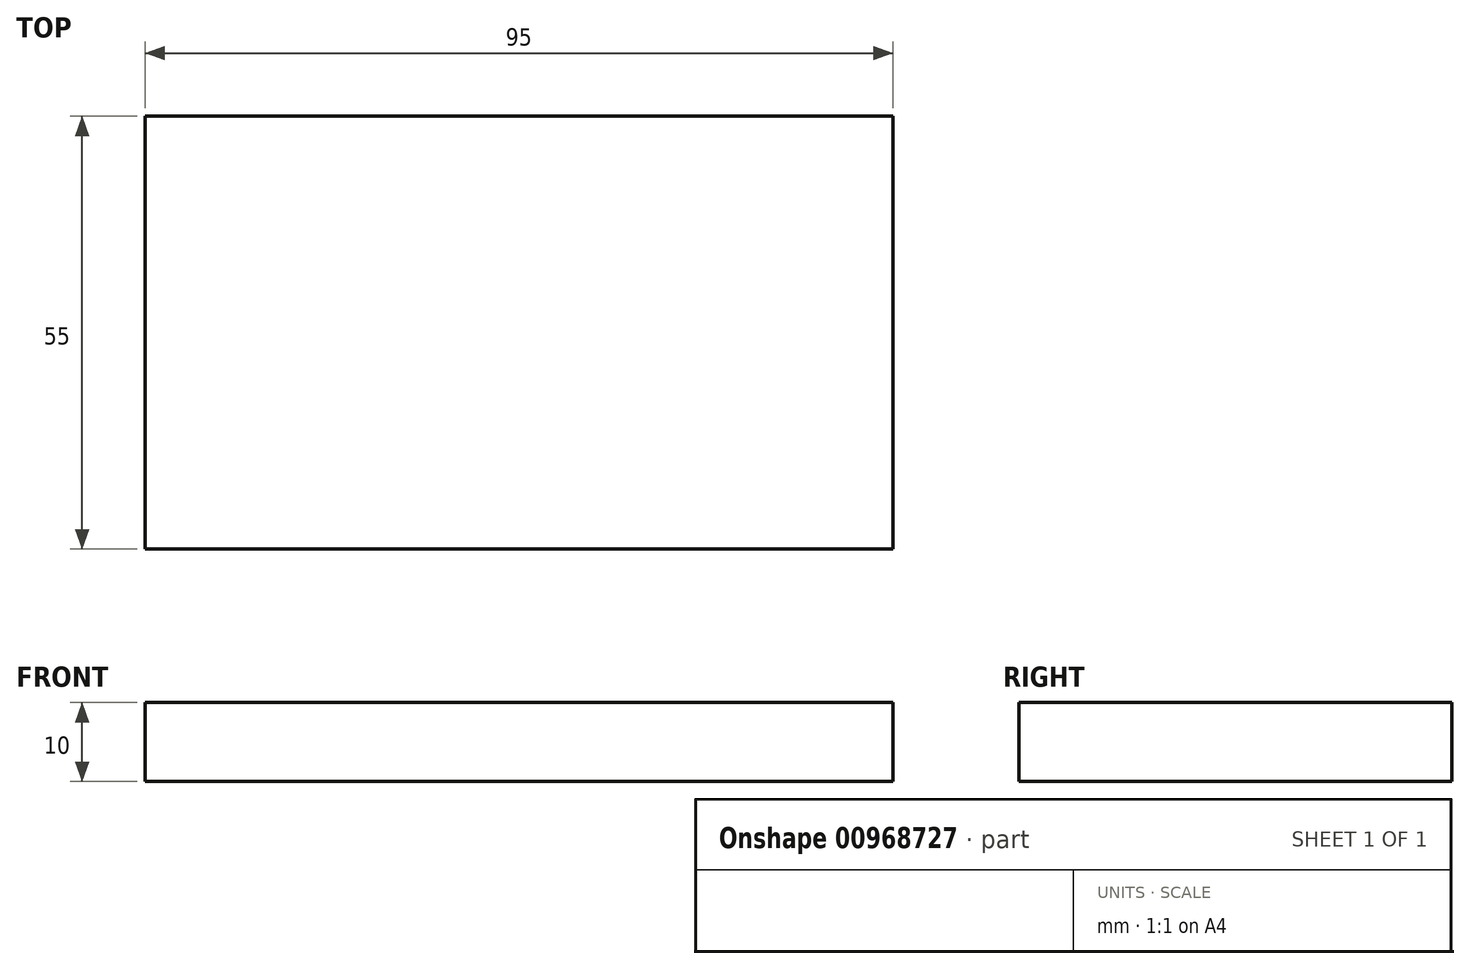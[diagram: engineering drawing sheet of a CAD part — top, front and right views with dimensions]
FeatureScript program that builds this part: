
annotation { "Feature Type Name" : "Feature", "Feature Type Description" : "" }
export const myFeature = defineFeature(function(context is Context, id is Id, definition is map)
    precondition{}
    {
        {
            var Q0;
            Q0=qCreatedBy(makeId("Front.planeOp"),FACE);
            var sketch = newSketch(context, id + "F0", { "sketchPlane" : qUnion([Q0])});
            skLineSegment(sketch, "E0.bottom", {"start": v(-27.99, 0) * mm, "end": v(67.01, 0) * mm});
            skLineSegment(sketch, "E0.top", {"start": v(-27.99, 10) * mm, "end": v(67.01, 10) * mm});
            skLineSegment(sketch, "E0.left", {"start": v(-27.99, 0) * mm, "end": v(-27.99, 10) * mm});
            skLineSegment(sketch, "E0.right", {"start": v(67.01, 0) * mm, "end": v(67.01, 10) * mm});
            skSolve(sketch);
        }
        {
            var Q0;
            Q0=sQuery(id+"F0.wireOp",EDGE,"E0.bottom");
            extrude(context, id + "F1", {"bodyType" : ToolBodyType.SURFACE, "surfaceEntities" : qUnion([Q0]), "oppositeDirection" : true, "depth" : 55 * mm, "offsetDistance" : 25 * mm});
        }
        {
            var Q0;
            Q0=makeQuery(id+"F1.opExtrude","SWEPT_FACE",FACE,{"disambiguationData":[OSD([sQuery(id+"F0.wireOp",EDGE,"E0.bottom")])]});
            extrude(context, id + "F2", {"entities" : qUnion([Q0]), "depth" : 10 * mm, "offsetDistance" : 25 * mm});
        }
    });
